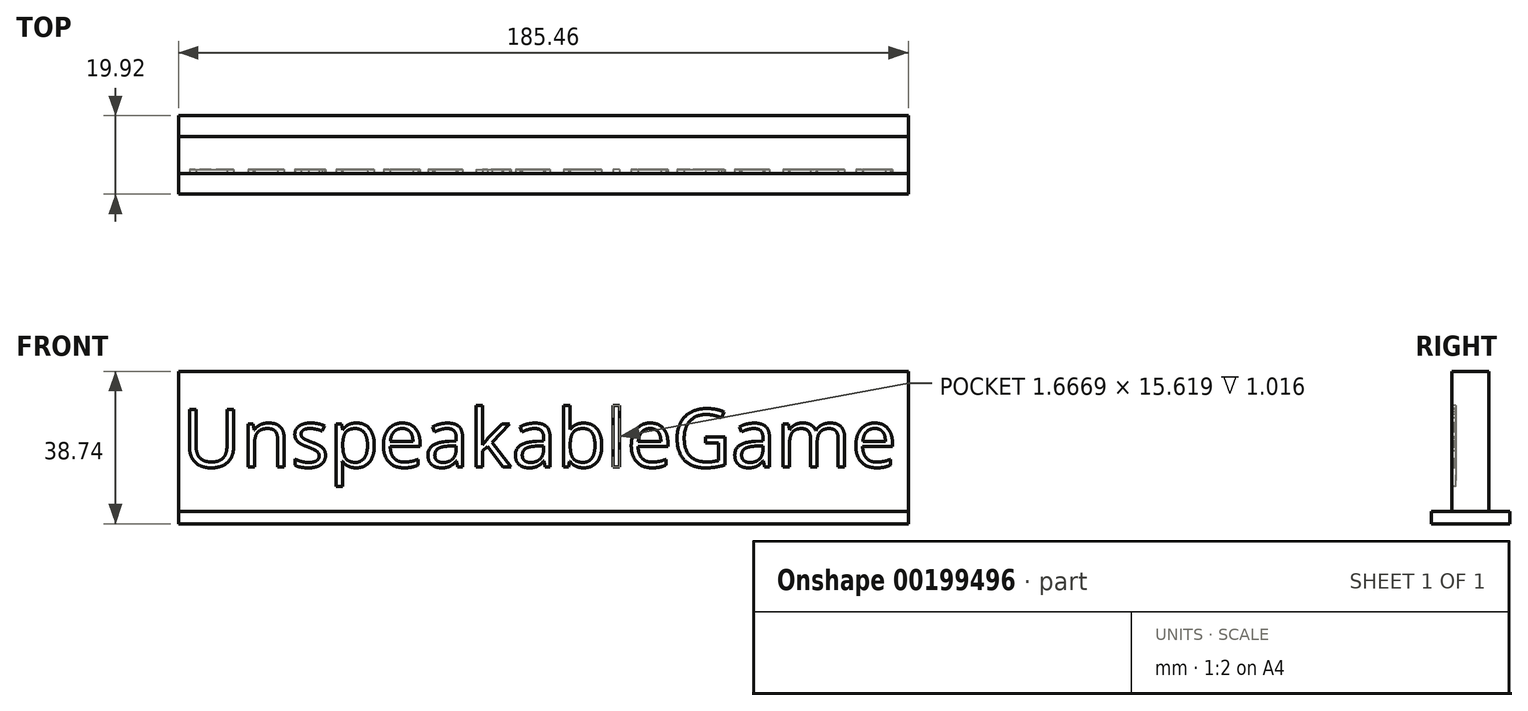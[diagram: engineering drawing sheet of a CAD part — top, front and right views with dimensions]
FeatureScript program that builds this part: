
annotation { "Feature Type Name" : "Feature", "Feature Type Description" : "" }
export const myFeature = defineFeature(function(context is Context, id is Id, definition is map)
    precondition{}
    {
        {
            var Q0;
            Q0=qCreatedBy(makeId("Front.planeOp"),FACE);
            var sketch = newSketch(context, id + "F0", { "sketchPlane" : qUnion([Q0])});
            skLineSegment(sketch, "E0.bottom", {"start": v(-92.7, 17.8) * mm, "end": v(92.71, 17.8) * mm});
            skPoint(sketch, "E0.middle", {"position": v(0, 0) * mm});
            skPoint(sketch, "E0.top.start.orphan", {"position": v(-92.7, -17.8) * mm});
            skPoint(sketch, "E1.orphan", {"position": v(90.12, -17.8) * mm});
            skLineSegment(sketch, "E2.bottom", {"start": v(-92.7, -17.8) * mm, "end": v(92.7, -17.8) * mm});
            skLineSegment(sketch, "E2.top", {"start": v(-92.7, 17.8) * mm, "end": v(92.7, 17.8) * mm});
            skLineSegment(sketch, "E2.left", {"start": v(-92.7, -17.8) * mm, "end": v(-92.7, 17.8) * mm});
            skLineSegment(sketch, "E2.right", {"start": v(92.7, -17.8) * mm, "end": v(92.7, 17.8) * mm});
            skPoint(sketch, "E0.left.end.orphan", {"position": v(-91.41, 0) * mm});
            skPoint(sketch, "E0.right.end.orphan", {"position": v(91.41, 0) * mm});
            skPoint(sketch, "E3.orphan", {"position": v(-90.12, 17.8) * mm});
            skSolve(sketch);
        }
        {
            var Q0;
            Q0 = qSketchRegion(id + "F0", true);
            extrude(context, id + "F1", {"entities" : qUnion([Q0]), "depth" : 9.4 * mm});
        }
        {
            var Q0;
            Q0=makeQuery(id+"F1.opExtrude","CAP_FACE",FACE,{"disambiguationData":[OSD([sQuery(id+"F0.wireOp",EDGE,"E2.bottom"),sQuery(id+"F0.wireOp",EDGE,"E2.top"),sQuery(id+"F0.wireOp",EDGE,"E2.left"),sQuery(id+"F0.wireOp",EDGE,"E2.right")])],"isStart":false});
            var sketch = newSketch(context, id + "F2", { "sketchPlane" : qUnion([Q0])});
            skText(sketch, "E4", { "text": "UnspeakableGame", "fontName": "OpenSans-Regular.ttf"});
            const initialGuessF2  = {"E4": [-0.09179, -0.00653, 1, 0, 0.0148]};
            skSetInitialGuess(sketch, initialGuessF2);
            skSolve(sketch);
        }
        {
            var Q0;
            Q0 = qSketchRegion(id + "F2", true);
            extrude(context, id + "F3", {"entities" : qUnion([Q0]), "operationType" : NewBodyOperationType.REMOVE, "oppositeDirection" : true, "depth" : 1.02 * mm});
        }
        {
            var Q0;
            Q0=makeQuery(id+"F1.opExtrude","SWEPT_FACE",FACE,{"disambiguationData":[OSD([sQuery(id+"F0.wireOp",EDGE,"E2.bottom")])]});
            var sketch = newSketch(context, id + "F4", { "sketchPlane" : qUnion([Q0])});
            skLineSegment(sketch, "E5.bottom", {"start": v(92.73, 14.6) * mm, "end": v(-92.73, 14.6) * mm});
            skLineSegment(sketch, "E5.top", {"start": v(92.73, -5.32) * mm, "end": v(-92.73, -5.32) * mm});
            skLineSegment(sketch, "E5.left", {"start": v(92.73, 14.6) * mm, "end": v(92.73, -5.32) * mm});
            skLineSegment(sketch, "E5.right", {"start": v(-92.73, 14.6) * mm, "end": v(-92.73, -5.32) * mm});
            skPoint(sketch, "E5.middle", {"position": v(0, 4.64) * mm});
            skSolve(sketch);
        }
        {
            var Q0;
            Q0=makeQuery(id+"F4.imprint","IMPRINT",FACE,{"disambiguationData":[TD([[makeQuery(id+"F4.imprint","IMPRINT",EDGE,{"derivedFrom":sQuery(id+"F4.wireOp",EDGE,"E5.bottom")}),1.0]])]});
            var Q1;
            {var subQ0=sQuery(id+"F0.wireOp",EDGE,"E2.bottom");Q1=makeQuery(id+"F4.imprint","IMPRINT",FACE,{"disambiguationData":[TD([[makeQuery(id+"F4.imprint","IMPRINT",EDGE,{"derivedFrom":makeQuery(id+"F1.opExtrude","CAP_EDGE",EDGE,{"disambiguationData":[OSD([subQ0])],"isStart":true})}),1.0]])]});}
            extrude(context, id + "F5", {"entities" : qUnion([Q0, Q1]), "operationType" : NewBodyOperationType.ADD, "depth" : 3.12 * mm});
        }
    });
